# Revit family: Maxlogic akıllı adresli buton harici tip
name_source: partatom
category: Fire Alarm Devices
units: mm (PartAtom-declared; Revit-internal decimal feet)

## family parameters
Cut with Voids When Loaded = No
Host = Face
Maintain Annotation Orientation = Yes
OmniClass Number = 23.85.30.21
OmniClass Title = Environmental Detection/Registration
Part Type = Normal
Room Calculation Point = No
Round Connector Dimension = Use Diameter
Shared = No

## types (2) — shared parameters
Code Performance = EN 54-11 ve EN 54-17
Color = Kırmızı
Device Adress Setup = El tipi adresleme cihazı
Fax Number = (+)90 216 466 45 10
Installation Manual = https://mavilielektronik.com
Main Material = Red Plastic PC/ABS
Manufacturer = Mavili Elektronik Ticaret A.Ş.
Model = MaxLogic
Mounting height = Zeminden 1.4m yukarı (+/- 200mm)
Mounting surface = Duvara montaj
Nominal Depth = 71 mm
Nominal Height = 97,5 mm
Nominal Width = 93 mm
Operating temperature = (-30°C) - (+70°C)
Operating voltage range = 18-33V/DC
Operatonal Voltage (default) = 24 V/DC
Protection Sign = IP67
Protective Cover = PS200
Secondary Material = Plastic
URL = https://www.mavili.com.tr
Warranty Duration Labor = 2
Warranty Duration Parts = 2
Warranty Duration Unit = Year
Weight = 270 g
zero-valued in all types: Cost, Default Elevation

## per-type parameters (varying)
| type | Description | Product Code |
| Maxlogic Akıllı Adresli IP67 Resetlenebilir Buton | Akıllı Adresli IP67 Resetlenebilir Buton | ML-1730 |
| Maxlogic Akıllı Adresli Kısa Devre İzolatörlü IP67 Resetlenebilir Buton | Akıllı Adresli Kısa Devre İzolatörlü IP67 Resetlenebilir Buton | ML-1730.SCI |

## geometry (parser evidence)
native form markers: Sweep x2
no freeform markers — native parametric forms only
